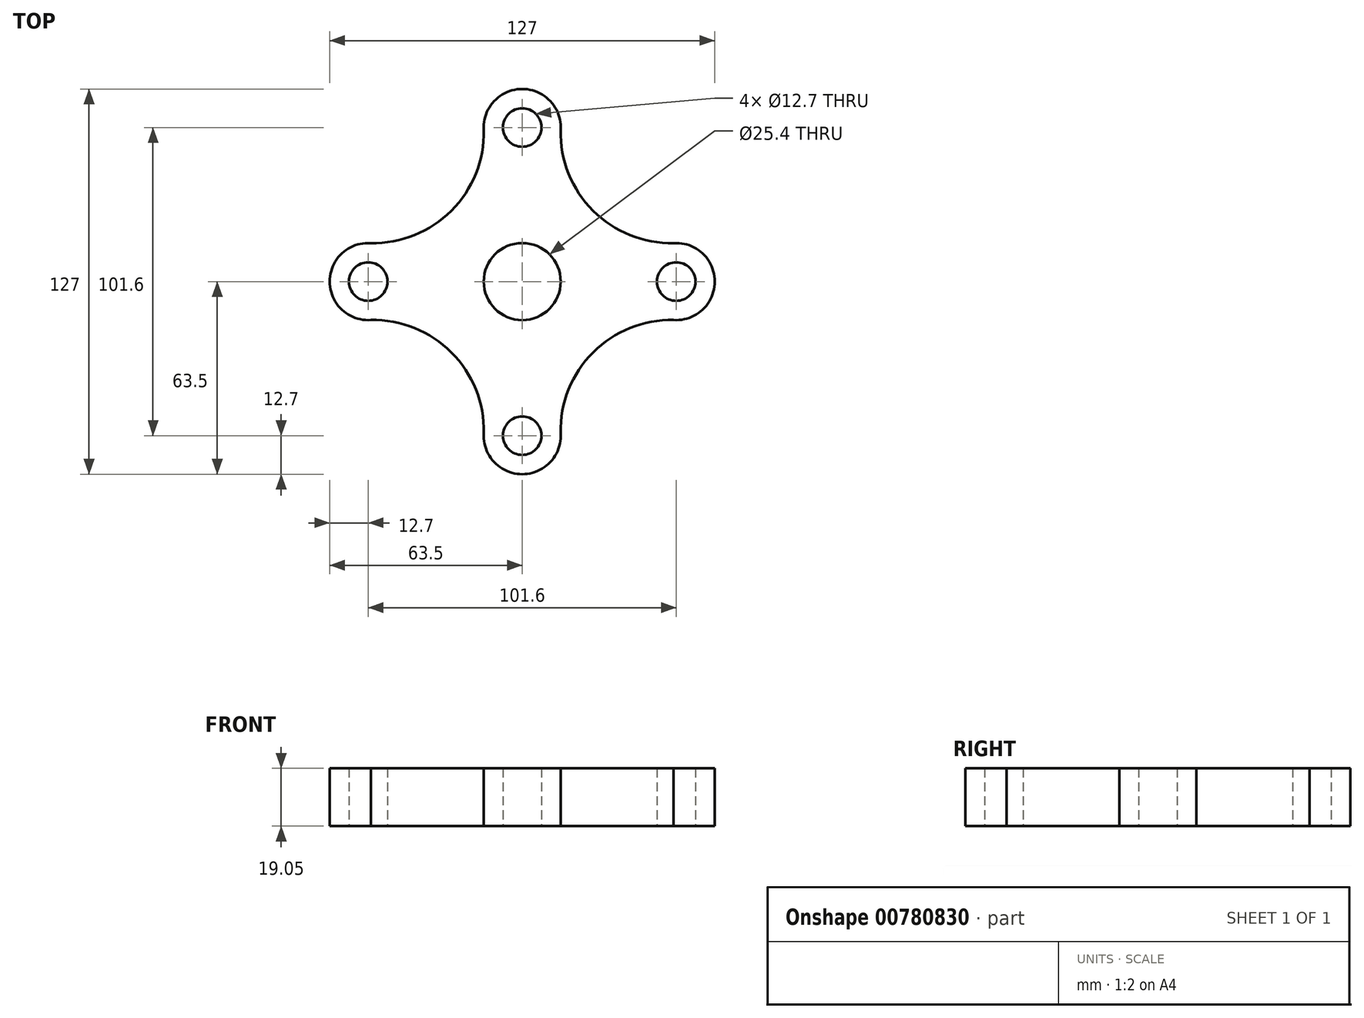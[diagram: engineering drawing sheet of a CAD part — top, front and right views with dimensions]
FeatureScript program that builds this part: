
annotation { "Feature Type Name" : "Feature", "Feature Type Description" : "" }
export const myFeature = defineFeature(function(context is Context, id is Id, definition is map)
    precondition{}
    {
        {
            var Q0;
            Q0=qCreatedBy(makeId("Top.planeOp"),FACE);
            var sketch = newSketch(context, id + "F0", { "sketchPlane" : qUnion([Q0])});
            skCircle(sketch, "E0", {"center": v(0, 0) * mm, "radius": 12.7 * mm});
            skCircle(sketch, "E1", {"center": v(0, 50.8) * mm, "radius": 6.35 * mm});
            skCircle(sketch, "E2", {"center": v(50.8, 0) * mm, "radius": 6.35 * mm});
            skCircle(sketch, "E3", {"center": v(0, -50.8) * mm, "radius": 6.35 * mm});
            skCircle(sketch, "E4", {"center": v(-50.8, 0) * mm, "radius": 6.35 * mm});
            skCircle(sketch, "E5", {"center": v(0, 50.8) * mm, "radius": 12.7 * mm});
            skCircle(sketch, "E6", {"center": v(50.8, 0) * mm, "radius": 12.7 * mm});
            skCircle(sketch, "E7", {"center": v(0, -50.8) * mm, "radius": 12.7 * mm});
            skCircle(sketch, "E8", {"center": v(-50.8, 0) * mm, "radius": 12.7 * mm});
            skLineSegment(sketch, "E9", {"start": v(0, 50.8) * mm, "end": v(16.91, 50.8) * mm});
            skLineSegment(sketch, "E10", {"start": v(0, 50.8) * mm, "end": v(-19.94, 50.8) * mm});
            skLineSegment(sketch, "E11", {"start": v(50.8, 0) * mm, "end": v(50.8, 17.16) * mm});
            skLineSegment(sketch, "E12", {"start": v(50.8, 0) * mm, "end": v(50.8, -18.17) * mm});
            skLineSegment(sketch, "E13", {"start": v(0, -50.8) * mm, "end": v(16.72, -50.8) * mm});
            skLineSegment(sketch, "E14", {"start": v(0, -50.8) * mm, "end": v(-17.07, -50.8) * mm});
            skLineSegment(sketch, "E15", {"start": v(-50.8, 0) * mm, "end": v(-50.8, -16.26) * mm});
            skLineSegment(sketch, "E16", {"start": v(-50.8, 0) * mm, "end": v(-50.8, 18.11) * mm});
            skArc(sketch, "E17", {"start": v(-50.8, 12.7) * mm, "mid": v(-23.36, 23.36) * mm, "end": v(-12.7, 50.8) * mm});
            skArc(sketch, "E18", {"start": v(12.7, 50.8) * mm, "mid": v(23.36, 23.36) * mm, "end": v(50.8, 12.7) * mm});
            skArc(sketch, "E19", {"start": v(50.8, -12.7) * mm, "mid": v(23.36, -23.36) * mm, "end": v(12.7, -50.8) * mm});
            skPoint(sketch, "E19.endSnap0", {"position": v(8.36, -50.8) * mm});
            skArc(sketch, "E20", {"start": v(-12.7, -50.8) * mm, "mid": v(-23.36, -23.36) * mm, "end": v(-50.8, -12.7) * mm});
            skSolve(sketch);
        }
        {
            var Q0;
            Q0 = qSketchRegion(id + "F0", true);
            extrude(context, id + "F1", {"entities" : qUnion([Q0]), "depth" : 19.05 * mm, "offsetDistance" : 25.4 * mm});
        }
    });
